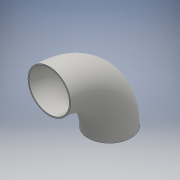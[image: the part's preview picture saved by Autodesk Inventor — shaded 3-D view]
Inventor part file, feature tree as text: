
AUTODESK INVENTOR PART (.ipt)
format: ipt  version: 2016 (Build 200138000, 138)  size: 155,648 bytes
history: native  units: mm
features: sweep x1, sketch x1
ambient origin geometry x8: Origin, YZ Plane, XZ Plane, XY Plane, X Axis, Y Axis, Z Axis, Center Point
bodies: Body1 (feature_tree)
feature tree (2):
  sweep  "Sweep2"
  sketch  "Sketch3"  dims[d14=324.0mm d15=9.27mm d16=0.0mm d17=0.0mm d18=457.0mm]
